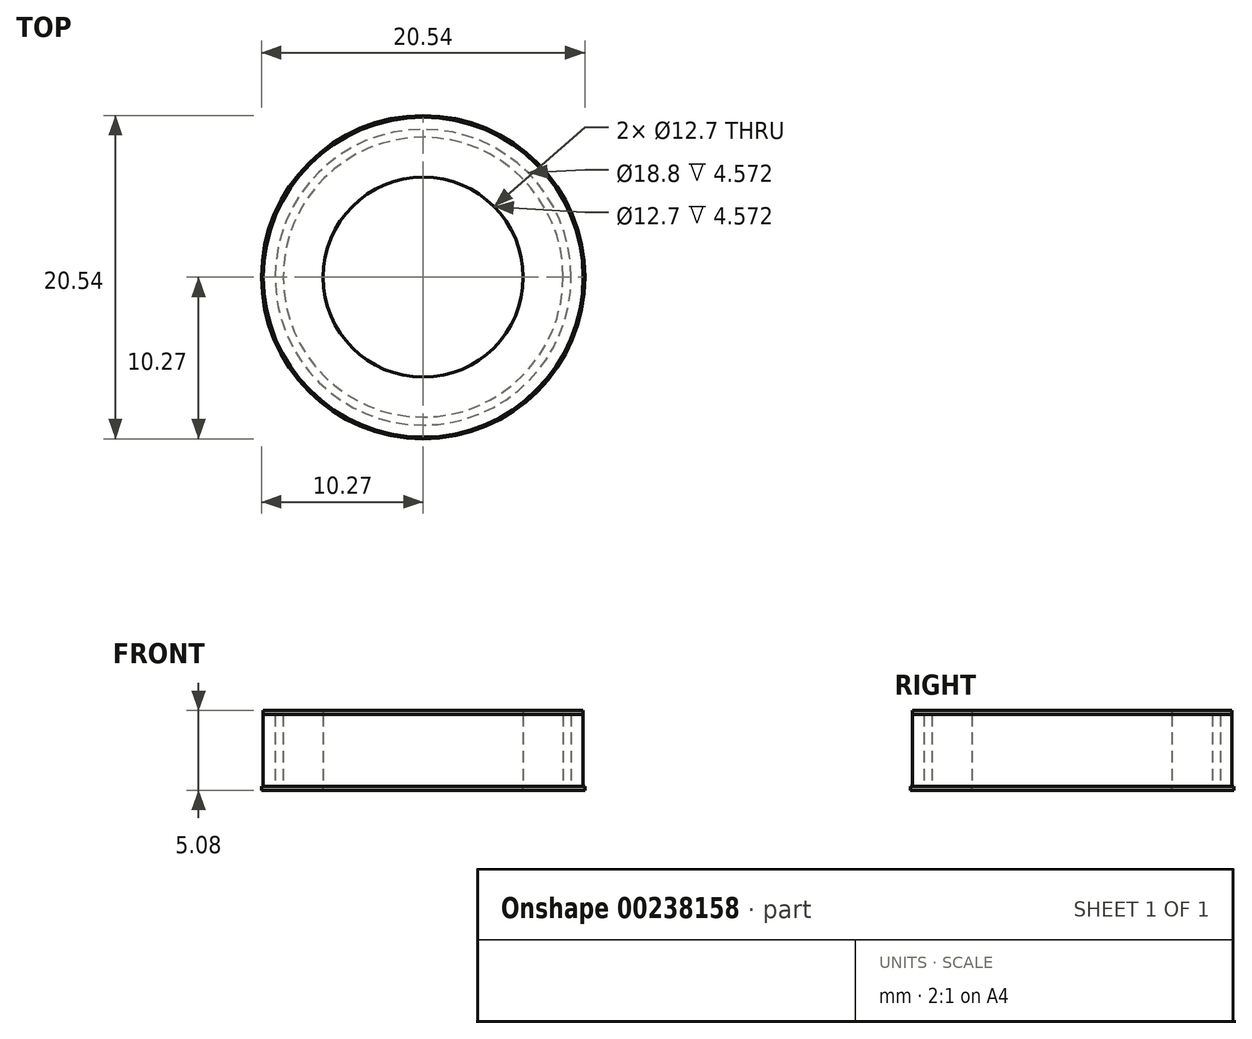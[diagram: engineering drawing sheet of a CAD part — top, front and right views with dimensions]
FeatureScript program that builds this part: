
annotation { "Feature Type Name" : "Feature", "Feature Type Description" : "" }
export const myFeature = defineFeature(function(context is Context, id is Id, definition is map)
    precondition{}
    {
        {
            var Q0;
            Q0=qCreatedBy(makeId("Top.planeOp"),FACE);
            var sketch = newSketch(context, id + "F0", { "sketchPlane" : qUnion([Q0])});
            skPoint(sketch, "E0", {"position": v(6.35, 0) * mm});
            skCircle(sketch, "E1", {"center": v(0, 0) * mm, "radius": 6.35 * mm});
            skPoint(sketch, "E2", {"position": v(8.9, 0) * mm});
            skCircle(sketch, "E3", {"center": v(0, 0) * mm, "radius": 8.9 * mm});
            skSolve(sketch);
        }
        {
            var Q0;
            Q0 = qSketchRegion(id + "F0", true);
            extrude(context, id + "F1", {"entities" : qUnion([Q0]), "depth" : 4.57 * mm});
        }
        {
            var Q0;
            Q0=qCreatedBy(makeId("Top.planeOp"),FACE);
            var sketch = newSketch(context, id + "F2", { "sketchPlane" : qUnion([Q0])});
            skPoint(sketch, "E4", {"position": v(9.4, 0) * mm});
            skPoint(sketch, "E5", {"position": v(10.16, 0) * mm});
            skCircle(sketch, "E6", {"center": v(0, 0) * mm, "radius": 9.4 * mm});
            skCircle(sketch, "E7", {"center": v(0, 0) * mm, "radius": 10.16 * mm});
            skSolve(sketch);
        }
        {
            var Q0;
            Q0 = qSketchRegion(id + "F2", true);
            extrude(context, id + "F3", {"entities" : qUnion([Q0]), "depth" : 4.57 * mm});
        }
        {
            var Q0;
            Q0=qCreatedBy(makeId("Top.planeOp"),FACE);
            var sketch = newSketch(context, id + "F4", { "sketchPlane" : qUnion([Q0])});
            skPoint(sketch, "E8", {"position": v(10.27, 0) * mm});
            skPoint(sketch, "E9", {"position": v(6.35, 0) * mm});
            skCircle(sketch, "E10", {"center": v(0, 0) * mm, "radius": 10.27 * mm});
            skCircle(sketch, "E11", {"center": v(0, 0) * mm, "radius": 6.35 * mm});
            skSolve(sketch);
        }
        {
            var Q0;
            Q0 = qSketchRegion(id + "F4", true);
            extrude(context, id + "F5", {"entities" : qUnion([Q0]), "oppositeDirection" : true, "depth" : 0.25 * mm});
        }
        {
            var Q0;
            Q0=makeQuery(id+"F1.opExtrude","CAP_FACE",FACE,{"disambiguationData":[OSD([sQuery(id+"F0.wireOp",EDGE,"E1"),sQuery(id+"F0.wireOp",EDGE,"E3")])],"isStart":false});
            var sketch = newSketch(context, id + "F6", { "sketchPlane" : qUnion([Q0])});
            skPoint(sketch, "E12", {"position": v(-6.35, 0) * mm});
            skPoint(sketch, "E13", {"position": v(-10.16, 0) * mm});
            skCircle(sketch, "E14", {"center": v(0, 0) * mm, "radius": 10.16 * mm});
            skCircle(sketch, "E15", {"center": v(0, 0) * mm, "radius": 6.35 * mm});
            skSolve(sketch);
        }
        {
            var Q0;
            Q0 = qSketchRegion(id + "F6", true);
            extrude(context, id + "F7", {"entities" : qUnion([Q0]), "depth" : 0.25 * mm});
        }
    });
